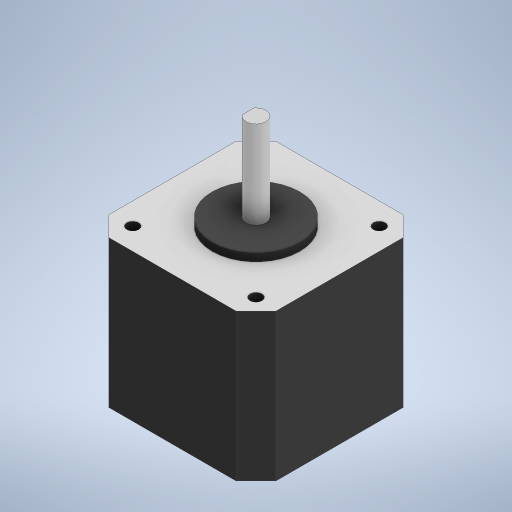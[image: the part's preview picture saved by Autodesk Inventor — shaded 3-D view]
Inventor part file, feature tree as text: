
AUTODESK INVENTOR PART (.ipt)
format: ipt  version: 2023 (Build 270158000, 158)  size: 266,240 bytes
history: native  units: mm
features: extrude x4, sketch x4, other x1
ambient origin geometry x8: Origin, YZ Plane, XZ Plane, XY Plane, X Axis, Y Axis, Z Axis, Center Point
bodies: Body1 (feature_tree)
feature tree (9):
  other  "솔리드1"
  extrude  "돌출1"  Depth=42.0mm
  extrude  "돌출2"  Depth=42.0mm
  extrude  "돌출3"  Depth=5.0mm
  extrude  "돌출4"  Depth=5.0mm
  sketch  "스케치1"
  sketch  "스케치2"
  sketch  "스케치3"
  sketch  "스케치4"
